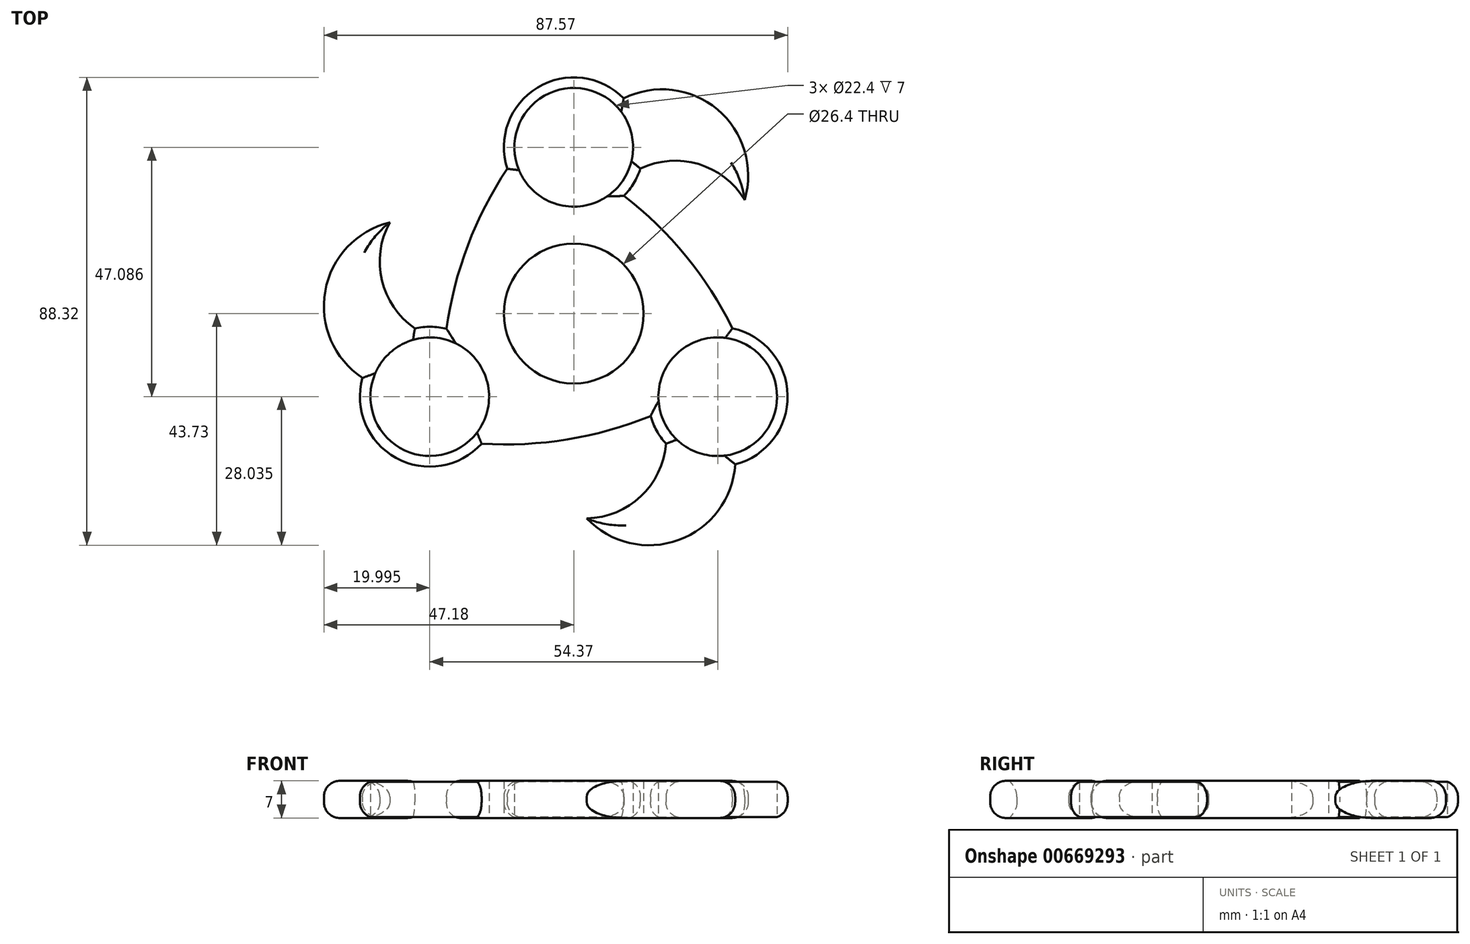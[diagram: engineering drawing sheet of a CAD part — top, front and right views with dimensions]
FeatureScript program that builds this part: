
annotation { "Feature Type Name" : "Feature", "Feature Type Description" : "" }
export const myFeature = defineFeature(function(context is Context, id is Id, definition is map)
    precondition{}
    {
        {
            var Q0;
            Q0=qCreatedBy(makeId("Top.planeOp"),FACE);
            var sketch = newSketch(context, id + "F0", { "sketchPlane" : qUnion([Q0])});
            skCircle(sketch, "E0", {"center": v(0, 0) * mm, "radius": 11.2 * mm});
            skCircle(sketch, "E1", {"center": v(0, 0) * mm, "radius": 13.2 * mm});
            skCircle(sketch, "E2", {"center": v(0, 31.4) * mm, "radius": 11.2 * mm});
            skCircle(sketch, "E3", {"center": v(0, 31.4) * mm, "radius": 13.2 * mm});
            skCircle(sketch, "E4.1.0", {"center": v(-27.19, -15.7) * mm, "radius": 13.2 * mm});
            skCircle(sketch, "E4.1.1", {"center": v(-27.19, -15.7) * mm, "radius": 11.2 * mm});
            skCircle(sketch, "E4.2.0", {"center": v(27.19, -15.7) * mm, "radius": 13.2 * mm});
            skCircle(sketch, "E4.2.1", {"center": v(27.19, -15.7) * mm, "radius": 11.2 * mm});
            skArc(sketch, "E5", {"start": v(-24.02, -2.88) * mm, "mid": v(-14.1, 10.64) * mm, "end": v(-12.56, 27.35) * mm});
            skArc(sketch, "E6.1.0", {"start": v(14.5, -19.36) * mm, "mid": v(-2.17, -17.52) * mm, "end": v(-17.4, -24.55) * mm});
            skArc(sketch, "E6.2.0", {"start": v(9.51, 22.24) * mm, "mid": v(16.26, 6.88) * mm, "end": v(29.96, -2.8) * mm});
            skArc(sketch, "E7", {"start": v(-12.56, 27.35) * mm, "mid": v(-20, 12.88) * mm, "end": v(-24.02, -2.88) * mm});
            skArc(sketch, "E8.1.0", {"start": v(-17.4, -24.55) * mm, "mid": v(-1.15, -23.76) * mm, "end": v(14.5, -19.36) * mm});
            skArc(sketch, "E8.2.0", {"start": v(29.96, -2.8) * mm, "mid": v(21.15, 10.88) * mm, "end": v(9.51, 22.24) * mm});
            skArc(sketch, "E9", {"start": v(32.27, 21.46) * mm, "mid": v(27.12, 38.53) * mm, "end": v(9.42, 40.63) * mm});
            skArc(sketch, "E10", {"start": v(32.27, 21.46) * mm, "mid": v(23.56, 28.22) * mm, "end": v(12.57, 27.36) * mm});
            skArc(sketch, "E11.1.0", {"start": v(-34.72, 17.21) * mm, "mid": v(-46.93, 4.22) * mm, "end": v(-39.9, -12.16) * mm});
            skArc(sketch, "E11.1.1", {"start": v(-34.72, 17.21) * mm, "mid": v(-36.22, 6.3) * mm, "end": v(-29.98, -2.8) * mm});
            skArc(sketch, "E11.2.0", {"start": v(2.45, -38.68) * mm, "mid": v(19.8, -42.75) * mm, "end": v(30.48, -28.48) * mm});
            skArc(sketch, "E11.2.1", {"start": v(2.45, -38.68) * mm, "mid": v(12.66, -34.52) * mm, "end": v(17.4, -24.57) * mm});
            skArc(sketch, "E12", {"start": v(33.6, -4.16) * mm, "mid": v(30.94, 8.4) * mm, "end": v(19.18, 13.6) * mm});
            skArc(sketch, "E13.1.0", {"start": v(-13.2, 31.18) * mm, "mid": v(-22.75, 22.59) * mm, "end": v(-21.37, 9.81) * mm});
            skArc(sketch, "E13.2.0", {"start": v(-20.4, -27.02) * mm, "mid": v(-8.19, -31) * mm, "end": v(2.19, -23.4) * mm});
            skSolve(sketch);
        }
        {
            var Q0;
            Q0=makeQuery(id+"F0.imprint","IMPRINT",FACE,{"disambiguationData":[TD([[makeQuery(id+"F0.imprint","IMPRINT",EDGE,{"derivedFrom":sQuery(id+"F0.wireOp",EDGE,"E1")}),-1.0]])]});
            var Q1;
            Q1=makeQuery(id+"F0.imprint","IMPRINT",FACE,{"disambiguationData":[TD([[makeQuery(id+"F0.imprint","IMPRINT",EDGE,{"derivedFrom":sQuery(id+"F0.wireOp",EDGE,"E5")}),1.0]])]});
            var Q2;
            Q2=makeQuery(id+"F0.imprint","IMPRINT",FACE,{"disambiguationData":[TD([[makeQuery(id+"F0.imprint","IMPRINT",EDGE,{"derivedFrom":sQuery(id+"F0.wireOp",EDGE,"E6.2.0")}),1.0]])]});
            var Q3;
            Q3=makeQuery(id+"F0.imprint","IMPRINT",FACE,{"disambiguationData":[TD([[makeQuery(id+"F0.imprint","IMPRINT",EDGE,{"derivedFrom":sQuery(id+"F0.wireOp",EDGE,"E6.1.0")}),1.0]])]});
            var Q4;
            Q4=makeQuery(id+"F0.imprint","IMPRINT",FACE,{"disambiguationData":[TD([[makeQuery(id+"F0.imprint","IMPRINT",EDGE,{"derivedFrom":sQuery(id+"F0.wireOp",EDGE,"E4.2.1")}),-1.0]])]});
            var Q5;
            {var subQ0=sQuery(id+"F0.wireOp",EDGE,"E11.2.0");Q5=makeQuery(id+"F0.imprint","IMPRINT",FACE,{"disambiguationData":[TD([[makeQuery(id+"F0.imprint","IMPRINT",EDGE,{"derivedFrom":subQ0}),1.0]])]});}
            var Q6;
            {var subQ0=sQuery(id+"F0.wireOp",EDGE,"E9");Q6=makeQuery(id+"F0.imprint","IMPRINT",FACE,{"disambiguationData":[TD([[makeQuery(id+"F0.imprint","IMPRINT",EDGE,{"derivedFrom":subQ0}),1.0]])]});}
            var Q7;
            Q7=makeQuery(id+"F0.imprint","IMPRINT",FACE,{"disambiguationData":[TD([[makeQuery(id+"F0.imprint","IMPRINT",EDGE,{"derivedFrom":sQuery(id+"F0.wireOp",EDGE,"E2")}),-1.0]])]});
            var Q8;
            {var subQ0=sQuery(id+"F0.wireOp",EDGE,"E11.1.0");Q8=makeQuery(id+"F0.imprint","IMPRINT",FACE,{"disambiguationData":[TD([[makeQuery(id+"F0.imprint","IMPRINT",EDGE,{"derivedFrom":subQ0}),1.0]])]});}
            var Q9;
            Q9=makeQuery(id+"F0.imprint","IMPRINT",FACE,{"disambiguationData":[TD([[makeQuery(id+"F0.imprint","IMPRINT",EDGE,{"derivedFrom":sQuery(id+"F0.wireOp",EDGE,"E4.1.1")}),-1.0]])]});
            extrude(context, id + "F1", {"entities" : qUnion([Q0, Q1, Q2, Q3, Q4, Q5, Q6, Q7, Q8, Q9]), "depth" : 7 * mm, "offsetDistance" : 25 * mm});
        }
        {
            var Q0;
            {var subQ0=sQuery(id+"F0.wireOp",EDGE,"E4.1.0");var subQ1=makeQuery(id+"F0.imprint","IMPRINT",VERTEX,{"derivedFrom":subQ0});Q0=makeQuery(id+"F1.opExtrude","CAP_EDGE",EDGE,{"disambiguationData":[OSD([subQ0]),TDD([makeQuery(id+"F0.imprint","IMPRINT",EDGE,{"disambiguationData":[TD([[subQ1,1.0]])],"derivedFrom":subQ0}),makeQuery(id+"F0.imprint","IMPRINT",EDGE,{"disambiguationData":[TD([[subQ1,-1.0]])],"derivedFrom":subQ0})])],"isStart":false});}
            var Q1;
            {var subQ0=sQuery(id+"F0.wireOp",EDGE,"E4.1.0");Q1=makeQuery(id+"F1.opExtrude","CAP_EDGE",EDGE,{"disambiguationData":[OSD([subQ0]),TDD([makeQuery(id+"F0.imprint","IMPRINT",EDGE,{"disambiguationData":[TD([[makeQuery(id+"F0.imprint","INTERSECT",VERTEX,{"derivedFrom":[subQ0,sQuery(id+"F0.wireOp",EDGE,"E11.1.1")]}),1.0]])],"derivedFrom":subQ0})])],"isStart":false});}
            var Q2;
            Q2=makeQuery(id+"F1.opExtrude","CAP_EDGE",EDGE,{"disambiguationData":[OSD([sQuery(id+"F0.wireOp",EDGE,"E7")])],"isStart":false});
            var Q3;
            {var subQ0=sQuery(id+"F0.wireOp",EDGE,"E3");var subQ1=makeQuery(id+"F0.imprint","IMPRINT",VERTEX,{"derivedFrom":subQ0});Q3=makeQuery(id+"F1.opExtrude","CAP_EDGE",EDGE,{"disambiguationData":[OSD([subQ0]),TDD([makeQuery(id+"F0.imprint","IMPRINT",EDGE,{"disambiguationData":[TD([[subQ1,1.0]])],"derivedFrom":subQ0}),makeQuery(id+"F0.imprint","IMPRINT",EDGE,{"disambiguationData":[TD([[subQ1,-1.0]])],"derivedFrom":subQ0})])],"isStart":false});}
            var Q4;
            {var subQ0=sQuery(id+"F0.wireOp",EDGE,"E3");Q4=makeQuery(id+"F1.opExtrude","CAP_EDGE",EDGE,{"disambiguationData":[OSD([subQ0]),TDD([makeQuery(id+"F0.imprint","IMPRINT",EDGE,{"disambiguationData":[TD([[makeQuery(id+"F0.imprint","INTERSECT",VERTEX,{"derivedFrom":[subQ0,sQuery(id+"F0.wireOp",EDGE,"E10")]}),1.0]])],"derivedFrom":subQ0})])],"isStart":false});}
            var Q5;
            Q5=makeQuery(id+"F1.opExtrude","CAP_EDGE",EDGE,{"disambiguationData":[OSD([sQuery(id+"F0.wireOp",EDGE,"E8.2.0")])],"isStart":false});
            var Q6;
            {var subQ0=sQuery(id+"F0.wireOp",EDGE,"E4.2.0");var subQ1=makeQuery(id+"F0.imprint","IMPRINT",VERTEX,{"derivedFrom":subQ0});Q6=makeQuery(id+"F1.opExtrude","CAP_EDGE",EDGE,{"disambiguationData":[OSD([subQ0]),TDD([makeQuery(id+"F0.imprint","IMPRINT",EDGE,{"disambiguationData":[TD([[subQ1,1.0]])],"derivedFrom":subQ0}),makeQuery(id+"F0.imprint","IMPRINT",EDGE,{"disambiguationData":[TD([[subQ1,-1.0]])],"derivedFrom":subQ0})])],"isStart":false});}
            var Q7;
            {var subQ0=sQuery(id+"F0.wireOp",EDGE,"E4.2.0");Q7=makeQuery(id+"F1.opExtrude","CAP_EDGE",EDGE,{"disambiguationData":[OSD([subQ0]),TDD([makeQuery(id+"F0.imprint","IMPRINT",EDGE,{"disambiguationData":[TD([[makeQuery(id+"F0.imprint","INTERSECT",VERTEX,{"derivedFrom":[subQ0,sQuery(id+"F0.wireOp",EDGE,"E11.2.1")]}),1.0]])],"derivedFrom":subQ0})])],"isStart":false});}
            var Q8;
            Q8=makeQuery(id+"F1.opExtrude","CAP_EDGE",EDGE,{"disambiguationData":[OSD([sQuery(id+"F0.wireOp",EDGE,"E8.1.0")])],"isStart":false});
            var Q9;
            Q9=makeQuery(id+"F1.opExtrude","CAP_EDGE",EDGE,{"disambiguationData":[OSD([sQuery(id+"F0.wireOp",EDGE,"E11.1.1")])],"isStart":false});
            var Q10;
            Q10=makeQuery(id+"F1.opExtrude","CAP_EDGE",EDGE,{"disambiguationData":[OSD([sQuery(id+"F0.wireOp",EDGE,"E11.1.0")])],"isStart":false});
            var Q11;
            Q11=makeQuery(id+"F1.opExtrude","CAP_EDGE",EDGE,{"disambiguationData":[OSD([sQuery(id+"F0.wireOp",EDGE,"E11.2.1")])],"isStart":false});
            var Q12;
            Q12=makeQuery(id+"F1.opExtrude","CAP_EDGE",EDGE,{"disambiguationData":[OSD([sQuery(id+"F0.wireOp",EDGE,"E11.2.0")])],"isStart":false});
            var Q13;
            Q13=makeQuery(id+"F1.opExtrude","CAP_EDGE",EDGE,{"disambiguationData":[OSD([sQuery(id+"F0.wireOp",EDGE,"E10")])],"isStart":false});
            var Q14;
            Q14=makeQuery(id+"F1.opExtrude","CAP_EDGE",EDGE,{"disambiguationData":[OSD([sQuery(id+"F0.wireOp",EDGE,"E9")])],"isStart":false});
            var Q15;
            Q15=makeQuery(id+"F1.opExtrude","CAP_EDGE",EDGE,{"disambiguationData":[OSD([sQuery(id+"F0.wireOp",EDGE,"E8.2.0")])],"isStart":true});
            var Q16;
            {var subQ0=sQuery(id+"F0.wireOp",EDGE,"E4.2.0");var subQ1=makeQuery(id+"F0.imprint","IMPRINT",VERTEX,{"derivedFrom":subQ0});Q16=makeQuery(id+"F1.opExtrude","CAP_EDGE",EDGE,{"disambiguationData":[OSD([subQ0]),TDD([makeQuery(id+"F0.imprint","IMPRINT",EDGE,{"disambiguationData":[TD([[subQ1,1.0]])],"derivedFrom":subQ0}),makeQuery(id+"F0.imprint","IMPRINT",EDGE,{"disambiguationData":[TD([[subQ1,-1.0]])],"derivedFrom":subQ0})])],"isStart":true});}
            var Q17;
            Q17=makeQuery(id+"F1.opExtrude","CAP_EDGE",EDGE,{"disambiguationData":[OSD([sQuery(id+"F0.wireOp",EDGE,"E11.2.0")])],"isStart":true});
            var Q18;
            Q18=makeQuery(id+"F1.opExtrude","CAP_EDGE",EDGE,{"disambiguationData":[OSD([sQuery(id+"F0.wireOp",EDGE,"E11.2.1")])],"isStart":true});
            var Q19;
            {var subQ0=sQuery(id+"F0.wireOp",EDGE,"E4.2.0");Q19=makeQuery(id+"F1.opExtrude","CAP_EDGE",EDGE,{"disambiguationData":[OSD([subQ0]),TDD([makeQuery(id+"F0.imprint","IMPRINT",EDGE,{"disambiguationData":[TD([[makeQuery(id+"F0.imprint","INTERSECT",VERTEX,{"derivedFrom":[subQ0,sQuery(id+"F0.wireOp",EDGE,"E11.2.1")]}),1.0]])],"derivedFrom":subQ0})])],"isStart":true});}
            var Q20;
            Q20=makeQuery(id+"F1.opExtrude","CAP_EDGE",EDGE,{"disambiguationData":[OSD([sQuery(id+"F0.wireOp",EDGE,"E8.1.0")])],"isStart":true});
            var Q21;
            {var subQ0=sQuery(id+"F0.wireOp",EDGE,"E4.1.0");var subQ1=makeQuery(id+"F0.imprint","IMPRINT",VERTEX,{"derivedFrom":subQ0});Q21=makeQuery(id+"F1.opExtrude","CAP_EDGE",EDGE,{"disambiguationData":[OSD([subQ0]),TDD([makeQuery(id+"F0.imprint","IMPRINT",EDGE,{"disambiguationData":[TD([[subQ1,1.0]])],"derivedFrom":subQ0}),makeQuery(id+"F0.imprint","IMPRINT",EDGE,{"disambiguationData":[TD([[subQ1,-1.0]])],"derivedFrom":subQ0})])],"isStart":true});}
            var Q22;
            Q22=makeQuery(id+"F1.opExtrude","CAP_EDGE",EDGE,{"disambiguationData":[OSD([sQuery(id+"F0.wireOp",EDGE,"E11.1.0")])],"isStart":true});
            var Q23;
            Q23=makeQuery(id+"F1.opExtrude","CAP_EDGE",EDGE,{"disambiguationData":[OSD([sQuery(id+"F0.wireOp",EDGE,"E11.1.1")])],"isStart":true});
            var Q24;
            {var subQ0=sQuery(id+"F0.wireOp",EDGE,"E4.1.0");Q24=makeQuery(id+"F1.opExtrude","CAP_EDGE",EDGE,{"disambiguationData":[OSD([subQ0]),TDD([makeQuery(id+"F0.imprint","IMPRINT",EDGE,{"disambiguationData":[TD([[makeQuery(id+"F0.imprint","INTERSECT",VERTEX,{"derivedFrom":[subQ0,sQuery(id+"F0.wireOp",EDGE,"E11.1.1")]}),1.0]])],"derivedFrom":subQ0})])],"isStart":true});}
            var Q25;
            Q25=makeQuery(id+"F1.opExtrude","CAP_EDGE",EDGE,{"disambiguationData":[OSD([sQuery(id+"F0.wireOp",EDGE,"E7")])],"isStart":true});
            var Q26;
            {var subQ0=sQuery(id+"F0.wireOp",EDGE,"E3");var subQ1=makeQuery(id+"F0.imprint","IMPRINT",VERTEX,{"derivedFrom":subQ0});Q26=makeQuery(id+"F1.opExtrude","CAP_EDGE",EDGE,{"disambiguationData":[OSD([subQ0]),TDD([makeQuery(id+"F0.imprint","IMPRINT",EDGE,{"disambiguationData":[TD([[subQ1,1.0]])],"derivedFrom":subQ0}),makeQuery(id+"F0.imprint","IMPRINT",EDGE,{"disambiguationData":[TD([[subQ1,-1.0]])],"derivedFrom":subQ0})])],"isStart":true});}
            var Q27;
            Q27=makeQuery(id+"F1.opExtrude","CAP_EDGE",EDGE,{"disambiguationData":[OSD([sQuery(id+"F0.wireOp",EDGE,"E9")])],"isStart":true});
            var Q28;
            Q28=makeQuery(id+"F1.opExtrude","CAP_EDGE",EDGE,{"disambiguationData":[OSD([sQuery(id+"F0.wireOp",EDGE,"E10")])],"isStart":true});
            var Q29;
            {var subQ0=sQuery(id+"F0.wireOp",EDGE,"E3");Q29=makeQuery(id+"F1.opExtrude","CAP_EDGE",EDGE,{"disambiguationData":[OSD([subQ0]),TDD([makeQuery(id+"F0.imprint","IMPRINT",EDGE,{"disambiguationData":[TD([[makeQuery(id+"F0.imprint","INTERSECT",VERTEX,{"derivedFrom":[subQ0,sQuery(id+"F0.wireOp",EDGE,"E10")]}),1.0]])],"derivedFrom":subQ0})])],"isStart":true});}
            fillet(context, id + "F2", {"entities" : qUnion([Q0, Q1, Q2, Q3, Q4, Q5, Q6, Q7, Q8, Q9, Q10, Q11, Q12, Q13, Q14, Q15, Q16, Q17, Q18, Q19, Q20, Q21, Q22, Q23, Q24, Q25, Q26, Q27, Q28, Q29]), "radius" : 3 * mm, "tangentPropagation" : true, "allowEdgeOverflow" : false});
        }
    });
